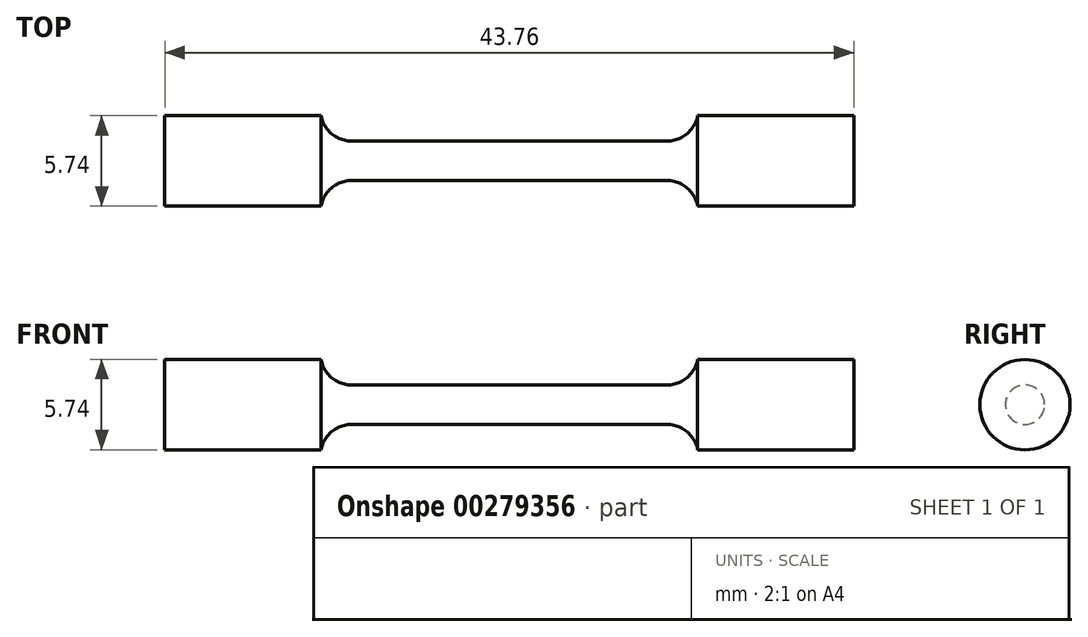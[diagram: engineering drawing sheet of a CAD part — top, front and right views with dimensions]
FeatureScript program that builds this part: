
annotation { "Feature Type Name" : "Feature", "Feature Type Description" : "" }
export const myFeature = defineFeature(function(context is Context, id is Id, definition is map)
    precondition{}
    {
        {
            var Q0;
            Q0=qCreatedBy(makeId("Front.planeOp"),FACE);
            var sketch = newSketch(context, id + "F0", { "sketchPlane" : qUnion([Q0])});
            skLineSegment(sketch, "E0", {"start": v(0, 1.25) * mm, "end": v(10, 1.25) * mm});
            skArc(sketch, "E1", {"start": v(10, 1.25) * mm, "mid": v(11.27, 1.7) * mm, "end": v(11.96, 2.87) * mm});
            skLineSegment(sketch, "E2", {"start": v(11.96, 2.87) * mm, "end": v(21.88, 2.87) * mm});
            skLineSegment(sketch, "E3", {"start": v(21.88, 2.87) * mm, "end": v(21.88, 0) * mm});
            skLineSegment(sketch, "E4.MirrorCS", {"start": v(0, 1.25) * mm, "end": v(-10, 1.25) * mm});
            skLineSegment(sketch, "E5.MirrorCS", {"start": v(-11.96, 2.87) * mm, "end": v(-21.88, 2.87) * mm});
            skArc(sketch, "E6.MirrorCS", {"start": v(-10, 1.25) * mm, "mid": v(-11.27, 1.7) * mm, "end": v(-11.96, 2.87) * mm});
            skLineSegment(sketch, "E7.MirrorCS", {"start": v(-21.88, 2.87) * mm, "end": v(-21.88, 0) * mm});
            skLineSegment(sketch, "E8", {"start": v(-21.88, 0) * mm, "end": v(21.88, 0) * mm});
            skSolve(sketch);
        }
        {
            var Q0;
            Q0 = qSketchRegion(id + "F0", true);
            var Q1;
            Q1=sQuery(id+"F0.wireOp",EDGE,"E8");
            revolve(context, id + "F1", {"entities" : qUnion([Q0]), "axis" : qUnion([Q1]), "revolveType" : RevolveType.FULL});
        }
    });
